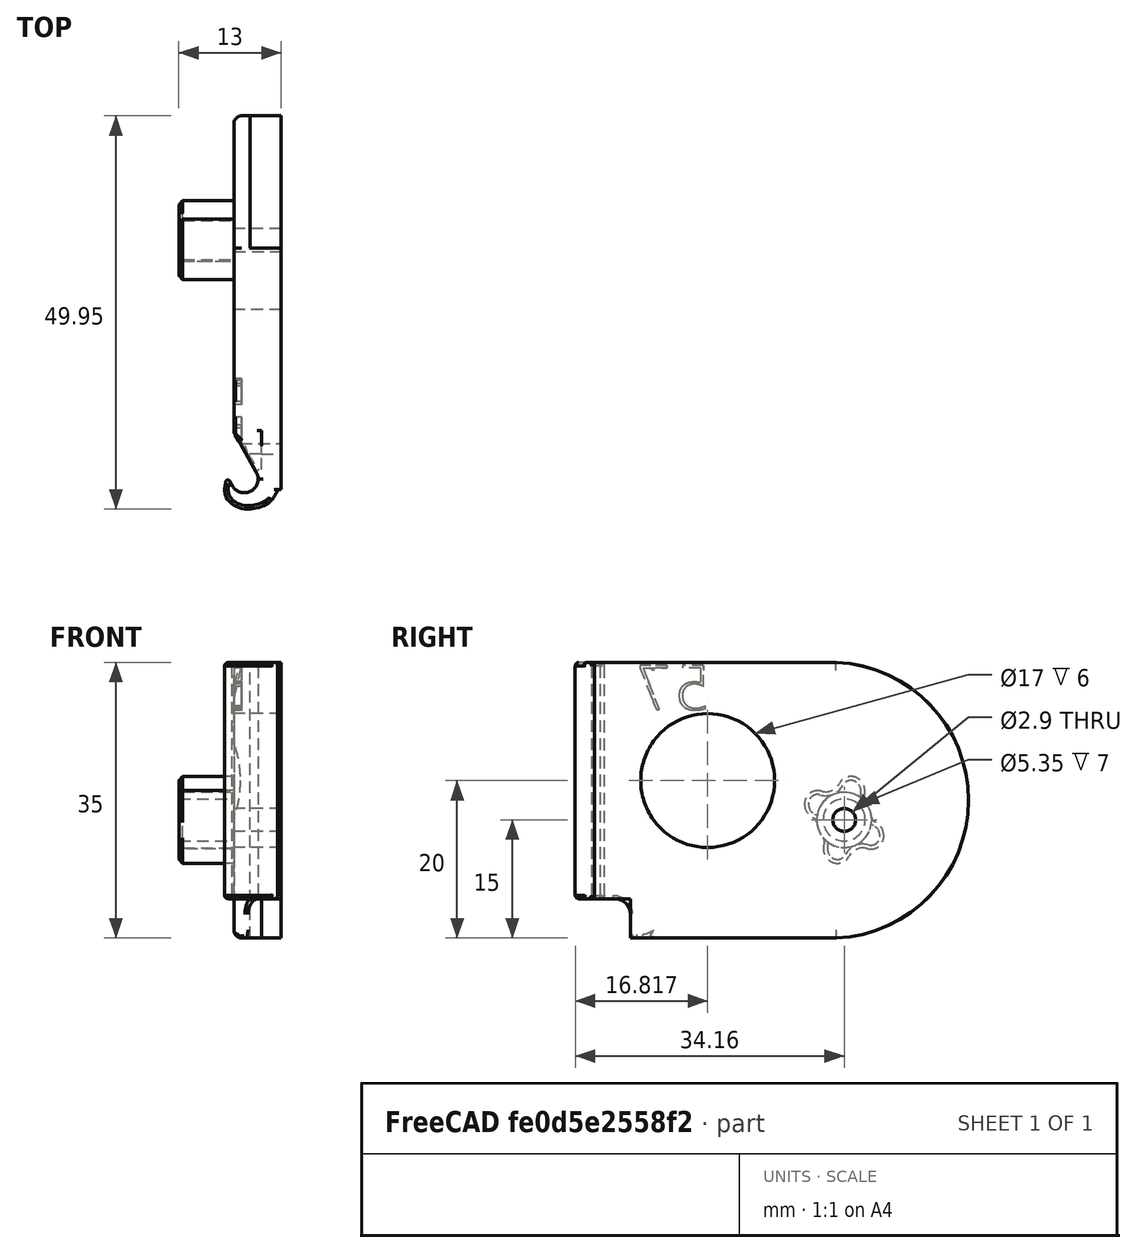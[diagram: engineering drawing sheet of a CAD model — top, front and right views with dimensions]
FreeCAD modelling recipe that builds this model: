
FCSTD DOCUMENT  (FreeCAD 0.18R)
Label: hinge-left-157deg-flat
License: All rights reserved
LicenseURL: http://en.wikipedia.org/wiki/All_rights_reserved
objects: App::FeaturePython×4, Part::FeaturePython×2, Part::Part2DObjectPython×1, Part::Extrusion×1, Part::Cut×1
note: 5 computed .brp shape members not serialized (recipe doc carries the construction recipe); baked Part::Feature solids carry a one-line shape summary decoded from their .brp

FEATURE [Part::FeaturePython] pillar_base_001  label="pillar-base_001"  # a2plus imported part (geometry in sourceFile) (typed FeaturePython)
  Placement = pos=(0.000608724,-0.509272,0.968843) rot=(-1,0,0;0.035081rad)
  a2p_Version = V0.1
  fixedPosition = false
  objectType = a2pPart
  sourceFile = ./parts/pillar-base.fcstd
  subassemblyImport = false
  timeLastImport = 1.60452e+09
  updateColors = true
FEATURE [Part::Part2DObjectPython] ShapeString  # Draft 2D object (typed FeaturePython)
  FontFile = <path>
  Placement = pos=(1.61,10.5,29) rot=(0.57735,-0.57735,-0.57735;2.0944rad)
  Size = 6
  String = 57
  Tracking = 0
FEATURE [Part::Extrusion] Extrude
  Base = -> ShapeString
  Dir = (-1,0,0)
  DirMode = 2
  FaceMakerClass = Part::FaceMakerBullseye
  LengthFwd = 2
  LengthRev = 0
  Solid = false
  Symmetric = false
FEATURE [Part::FeaturePython] bracket_left_flat_001  label="bracket-left-flat_001"  # a2plus imported part (geometry in sourceFile) (typed FeaturePython)
  a2p_Version = V0.1
  fixedPosition = true
  objectType = a2pPart
  sourceFile = ./parts/bracket-left-flat.fcstd
  subassemblyImport = false
  timeLastImport = 1.60454e+09
  updateColors = true
FEATURE [App::FeaturePython] axisCoincident_001  label="axisCoincident_001__bracket-left-flat_001"  # a2plus constraint (typed FeaturePython)
  Object1 = pillar_base_001
  Object2 = bracket_left_flat_001
  ParentTreeObject = -> pillar_base_001
  SubElement1 = Face17
  SubElement2 = Face48
  Suppressed = false
  Type = axial
  directionConstraint = 1
  lockRotation = false
FEATURE [App::FeaturePython] axisCoincident_001_mirror  label="axisCoincident_001__pillar-base_001"  # a2plus constraint (typed FeaturePython)
  Object1 = pillar_base_001
  Object2 = bracket_left_flat_001
  ParentTreeObject = -> bracket_left_flat_001
  SubElement1 = Face17
  SubElement2 = Face48
  Suppressed = false
  Type = axial
  directionConstraint = 1
  lockRotation = false
FEATURE [App::FeaturePython] planeCoincident_001  label="planeCoincident_001__bracket-left-flat_001"  # a2plus constraint (typed FeaturePython)
  Object1 = pillar_base_001
  Object2 = bracket_left_flat_001
  ParentTreeObject = -> pillar_base_001
  SubElement1 = Face1
  SubElement2 = Face72
  Suppressed = false
  Type = plane
  directionConstraint = 0
  offset = 0
FEATURE [App::FeaturePython] planeCoincident_001_mirror  label="planeCoincident_001__pillar-base_001"  # a2plus constraint (typed FeaturePython)
  Object1 = pillar_base_001
  Object2 = bracket_left_flat_001
  ParentTreeObject = -> bracket_left_flat_001
  SubElement1 = Face1
  SubElement2 = Face72
  Suppressed = false
  Type = plane
  directionConstraint = 0
  offset = 0
FEATURE [Part::Cut] Cut
  Base = -> bracket_left_flat_001
  Tool = -> Extrude
note: 1 file-system path scrubbed to <path> (originals preserved in the JSON sidecar)
